# Revit family: HARMANN - ROH_PS
name_source: partatom
category: Mechanical Equipment
units: mm (PartAtom-declared; Revit-internal decimal feet)

## family parameters
Always vertical = Yes
Cut with Voids When Loaded = No
Maintain Annotation Orientation = No
OmniClass Number = 23.75.00.00
OmniClass Title = Climate Control (HVAC)
Part Type = Normal
Room Calculation Point = No
Round Connector Dimension = Use Diameter
Shared = No
Work Plane-Based = No

## types (5) — shared parameters
Autor = https://www.archispace.com
Description = Dachowy wentylator z wyrzutem poziomym
Manufacturer = "Harmann Polska Sp. z o.o."
Opc Brak podstawy = Podstawa : Brak podstawy
Opc Podstawa Dachowa DSF AL = Podstawa : DSF AL
Opc Podstawa Dachowa DSS AL = Podstawa : DSS AL
Podstawa A = Podstawa : Brak podstawy
Podstawa B = Podstawa : DSF AL
Podstawa C = Podstawa : DSS AL
Zasilanie Częstotliwość Nominalna fnom = 50 Hz
zero-valued in all types: Default Elevation

## per-type parameters (varying)
| type | Akc DAF | Akc DAS | Akc DKP | Akc DSF AL | Akc DSS AL | Akc DVK | Ciśnienie akustyczne nominalne obudowa Lpa | DN | Masa | Masa mmax | Moc akustyczna nominalna obudowa Lwa | Numer artykułu | Obroty nominalne nnom | Powietrze Przepływ Maksymalny Qmax | Powietrze ciśnienie statyczne maksymalne dPmax | ROH.PS 4- | Regulacja | Temperatura pracy ciągłej maksymalna T | Zasilanie Częstotliwość Maksymalna fmax | Zasilanie Częstotliwość Minimalna fmin | Zasilanie Ilość faz | Zasilanie Moc maksymalna Pmax | Zasilanie napięcie nominalne Unom | Zasilanie natężenie maksymalne Imax |
| ROH.PS 4-450/6600S | HARMANN - Akcesoria - DAF : 400 | HARMANN - Akcesoria - DAS : 400 | HARMANN - Akcesoria - DKP : 450 | HARMANN - Akcesoria - DSF AL : DSF AL 450 | HARMANN - Akcesoria - DSS AL : DSS AL 455 | HARMANN - Akcesoria - DVK : 400 | 55 dB(A) | 400 mm  [stored 1.31234 ft] | 45.70 kg | 64.70 kg | 78 dB(A) | 16087800 | 1440.000 RPM | 6590.00 m³/h | 680.0 Pa | HARMANN - Akcesoria - ROH_PS 4 : ROH.PS 4-450/6600S | napięciowa 5 stopniowa | 55 °C | 50 Hz | 50 Hz | 1 | 809 W | 230 V | 4 A |
| ROH.PS 4-500/8400S | HARMANN - Akcesoria - DAF : 400 | HARMANN - Akcesoria - DAS : 400 | HARMANN - Akcesoria - DKP : 450 | HARMANN - Akcesoria - DSF AL : DSF AL 450 | HARMANN - Akcesoria - DSS AL : DSS AL 455 | HARMANN - Akcesoria - DVK : 400 | 61 dB(A) | 400 mm  [stored 1.31234 ft] | 53.30 kg | 72.30 kg | 84 dB(A) | 16088000 | 1460.000 RPM | 8420.00 m³/h | 850.0 Pa | HARMANN - Akcesoria - ROH_PS 4 : ROH.PS 4-500/8400S | napięciowa 5 stopniowa | 55 °C | 50 Hz | 50 Hz | 1 | 1383 W | 230 V | 8 A |
| ROH.PS 4-450/7600T | HARMANN - Akcesoria - DAF : 400 | HARMANN - Akcesoria - DAS : 400 | HARMANN - Akcesoria - DKP : 450 | HARMANN - Akcesoria - DSF AL : DSF AL 450 | HARMANN - Akcesoria - DSS AL : DSS AL 455 | HARMANN - Akcesoria - DVK : 400 | 62 dB(A) | 400 mm  [stored 1.31234 ft] | 49.00 kg | 68.00 kg | 85 dB(A) | 16335200 | 1640.000 RPM | 7650.00 m³/h | 870.0 Pa | HARMANN - Akcesoria - ROH_PS 4 : ROH.PS 4-450/7600T | Przemiennik częstotliwości | 60 °C | 55 Hz | 20 Hz | 3 | 1203 W | 400 V | 3 A |
| ROH.PS 4-500/9200T | HARMANN - Akcesoria - DAF : 400 | HARMANN - Akcesoria - DAS : 400 | HARMANN - Akcesoria - DKP : 450 | HARMANN - Akcesoria - DSF AL : DSF AL 450 | HARMANN - Akcesoria - DSS AL : DSS AL 455 | HARMANN - Akcesoria - DVK : 400 | 62 dB(A) | 400 mm  [stored 1.31234 ft] | 51.30 kg | 70.30 kg | 85 dB(A) | 16335300 | 1485.000 RPM | 9150.00 m³/h | 880.0 Pa | HARMANN - Akcesoria - ROH_PS 4 : ROH.PS 4-500/9200T | Przemiennik częstotliwości | 60 °C | 50 Hz | 20 Hz | 3 | 1462 W | 400 V | 3 A |
| ROH.PS 4-560/13900T | HARMANN - Akcesoria - DAF : 560 | HARMANN - Akcesoria - DAS : 560 | HARMANN - Akcesoria - DKP : 560 | HARMANN - Akcesoria - DSF AL : DSF AL 560 | HARMANN - Akcesoria - DSS AL : DSS AL 560 | HARMANN - Akcesoria - DVK : 560 | 64 dB(A) | 560 mm  [stored 1.83727 ft] | 77.30 kg | 104.30 kg | 87 dB(A) | 16088200 | 1485.000 RPM | 13900.00 m³/h | 1120.0 Pa | HARMANN - Akcesoria - ROH_PS 4 : ROH.PS 4-560/13900T | Przemiennik częstotliwości | 60 °C | 50 Hz | 20 Hz | 3 | 2642 W | 400 V | 5 A |

note: column(s) folded — value = type name in every type: Model

note: [stored X ft] marks values corroborated as IEEE doubles in the binary element streams (Revit-internal decimal feet)

## geometry (parser evidence)
native form markers: Sweep x21
no freeform markers — native parametric forms only
